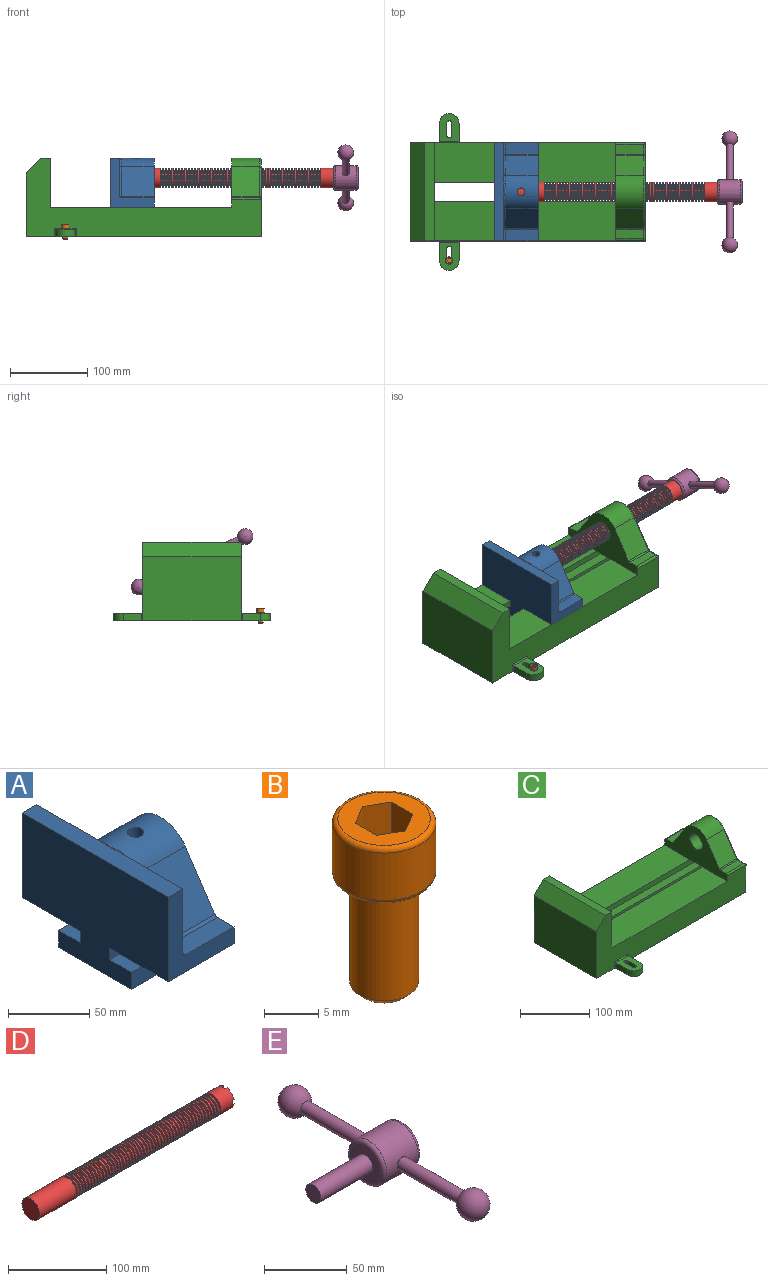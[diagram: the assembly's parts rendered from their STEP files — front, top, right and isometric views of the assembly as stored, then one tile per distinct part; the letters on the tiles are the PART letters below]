
ASSEMBLY  parts=5 mates=5
PART A: 36 faces, bbox 57.2x127x89 mm
  f0: plane 57.15x50.8mm, normal (0,0,-1), area 2903.2mm2, adj f6,f9,f10,f23
  f1: cylinder r=12.7mm len=44.45mm, axis (1,0,0), area 3464.3mm2, adj f6,f15,f16
  f2: plane 41.91x14.52mm, normal (0,0,1), area 608.5mm2, adj f6,f11,f24,f25
  f3: plane 51.86x48.26mm, normal (1,0,0), area 1495.7mm2, adj f8,f10,f31,f33,f35
  f4: plane 51.86x48.26mm, normal (1,0,0), area 1495.7mm2, adj f8,f11,f24,f28,f29
  f5: plane 57.15x50.8mm, normal (0,0,-1), area 2903.2mm2, adj f6,f9,f11,f22
  f6: plane 127x85.09mm, normal (1,0,0), area 5190.6mm2, adj f0,f1,f2,f5,f7,f10,f11,f12
  f7: plane 41.91x14.52mm, normal (0,0,1), area 608.5mm2, adj f6,f10,f30,f31
  f8: plane 127x12.7mm, normal (0,0,1), area 1612.9mm2, adj f3,f4,f9,f10,f11,f26,f34
  f9: plane 127x85.09mm, normal (-1,0,0), area 9096.8mm2, adj f0,f5,f8,f10,f11,f17,f18,f19
  f10: plane 63.5x57.15mm, normal (0,-1,0), area 1372.3mm2, adj f0,f3,f6,f7,f8,f9,f31
  f11: plane 63.5x57.15mm, normal (0,1,0), area 1372.3mm2, adj f2,f4,f5,f6,f8,f9,f24
  f12: plane 41.91x38.43mm, normal (0,-0.83,0.56), area 1939.2mm2, adj f6,f13,f30,f33
  f13: cylinder r=25.4mm len=44.45mm, axis (1,0,0), area 2026.5mm2, adj f6,f12,f14,f16,f26,f28,f34,f35
  f14: plane 41.91x38.43mm, normal (0,0.83,0.56), area 1939.2mm2, adj f6,f13,f25,f29
  f15: plane 25.4x25.4mm, normal (1,0,0), area 506.7mm2, adj f1
  f16: cylinder r=5.08mm len=13.76mm, axis (0,0,1), area 414mm2, adj f1,f13
  f17: plane 57.15x19.05mm, normal (0,0,1), area 1088.7mm2, adj f6,f9,f18,f23
  f18: plane 57.15x12.7mm, normal (0,-1,0), area 725.8mm2, adj f6,f9,f17,f19
  f19: plane 63.5x57.15mm, normal (0,0,-1), area 3629mm2, adj f6,f9,f18,f20
  f20: plane 57.15x12.7mm, normal (0,1,0), area 725.8mm2, adj f6,f9,f19,f21
  f21: plane 57.15x19.05mm, normal (0,0,1), area 1088.7mm2, adj f6,f9,f20,f22
  f22: plane 57.15x8.89mm, normal (0,1,0), area 508.1mm2, adj f5,f6,f9,f21
  f23: plane 57.15x8.89mm, normal (0,-1,0), area 508.1mm2, adj f0,f6,f9,f17
  f24: cylinder r=2.54mm len=14.52mm, axis (0,-1,0), area 57.9mm2, adj f2,f4,f11,f27
  f25: cylinder r=2.54mm len=41.91mm, axis (1,0,0), area 104.3mm2, adj f2,f6,f14,f27
  f26: bspline ~12.24x2.8mm, area 20.9mm2, adj f8,f13,f28
  f27: sphere r=2.54mm, area 6.3mm2, adj f24,f25,f29
  f28: torus R=27.94mm, axis (1,0,0), area 57.8mm2, adj f4,f13,f26,f29
  f29: cylinder r=2.54mm len=39.84mm, axis (0,-0.56,0.83), area 184.6mm2, adj f4,f14,f27,f28
  f30: cylinder r=2.54mm len=41.91mm, axis (1,0,0), area 104.3mm2, adj f6,f7,f12,f32
  f31: cylinder r=2.54mm len=14.52mm, axis (0,-1,0), area 57.9mm2, adj f3,f7,f10,f32
  f32: sphere r=2.54mm, area 6.3mm2, adj f30,f31,f33
  f33: cylinder r=2.54mm len=39.84mm, axis (0,-0.56,-0.83), area 184.6mm2, adj f3,f12,f32,f35
  f34: bspline ~12.24x2.8mm, area 20.9mm2, adj f8,f13,f35
  f35: torus R=27.94mm, axis (1,0,0), area 57.8mm2, adj f3,f13,f33,f34
PART B: 15 faces, bbox 10.3x10.3x19.1 mm
  f0: plane 8.51x8.51mm, normal (0,0,1), area 37.2mm2, adj f5,f6,f7,f8,f9,f10,f14
  f1: cylinder r=3.17mm len=11.94mm, axis (0,0,1), area 238.2mm2, adj f4,f12
  f2: plane 4.83x4.83mm, normal (0,0,-1), area 18.3mm2, adj f12
  f3: cylinder r=4.76mm len=9.53mm, axis (0,0,-1), area 159.6mm2, adj f13,f14
  f4: plane 8.51x8.51mm, normal (0,0,-1), area 25.2mm2, adj f1,f13
  f5: plane 4.83x2.38mm, normal (-0.5,-0.87,0), area 13.3mm2, adj f0,f6,f10,f11
  f6: plane 4.83x2.38mm, normal (0.5,-0.87,0), area 13.3mm2, adj f0,f5,f7,f11
  f7: plane 4.83x2.75mm, normal (1,0,0), area 13.3mm2, adj f0,f6,f8,f11
  f8: plane 4.83x2.38mm, normal (0.5,0.87,0), area 13.3mm2, adj f0,f7,f9,f11
  f9: plane 4.83x2.38mm, normal (-0.5,0.87,0), area 13.3mm2, adj f0,f8,f10,f11
  f10: plane 4.83x2.75mm, normal (-1,0,0), area 13.3mm2, adj f0,f5,f9,f11
  f11: plane 5.5x4.76mm, normal (0,0,1), area 19.6mm2, adj f5,f6,f7,f8,f9,f10
  f12: cone r=3.17mm half-angle=45deg, axis (0,0,1), area 18.9mm2, adj f1,f2
  f13: torus R=4.25mm, axis (0,0,1), area 23mm2, adj f3,f4
  f14: torus R=4.25mm, axis (0,0,1), area 23mm2, adj f0,f3
PART C: 61 faces, bbox 304.8x203.2x103.7 mm
  f0: plane 304.8x101.6mm, normal (0,1,0), area 13520.3mm2, adj f3,f4,f5,f6,f7,f8,f9,f16
  f1: plane 304.8x101.6mm, normal (0,-1,0), area 13520.3mm2, adj f2,f3,f5,f6,f7,f8,f9,f16
  f2: plane 234.95x50.8mm, normal (0,0,1), area 11935.5mm2, adj f1,f5,f16,f26
  f3: plane 127x99.06mm, normal (1,0,0), area 7097.5mm2, adj f0,f1,f9,f14,f17,f18,f19,f20
  f4: plane 234.95x50.8mm, normal (0,0,1), area 11935.5mm2, adj f0,f5,f16,f27
  f5: plane 127x101.6mm, normal (1,0,0), area 9516.1mm2, adj f0,f1,f2,f4,f6,f9,f18,f19
  f6: plane 127x12.7mm, normal (0,0,1), area 1612.9mm2, adj f0,f1,f5,f7
  f7: plane 127x19.05mm, normal (-0.71,0,0.71), area 3421.5mm2, adj f0,f1,f6,f8
  f8: plane 127x82.55mm, normal (-1,0,0), area 10483.8mm2, adj f0,f1,f7,f9
  f9: plane 304.8x203.2mm, normal (0,0,-1), area 33298.3mm2, adj f0,f1,f3,f5,f8,f21,f22,f39
  f10: plane 35.56x11.98mm, normal (0,0,1), area 426mm2, adj f16,f28,f29,f30
  f11: plane 38.43x35.56mm, normal (0,0.83,0.56), area 1645.4mm2, adj f12,f16,f29,f32
  f12: cylinder r=25.4mm len=42.19mm, axis (1,0,0), area 1770.2mm2, adj f11,f13,f16,f33
  f13: plane 38.43x35.56mm, normal (0,-0.83,0.56), area 1645.4mm2, adj f12,f16,f34,f35
  f14: cylinder r=12.7mm len=38.1mm, axis (1,0,0), area 3040.2mm2, adj f3,f16
  f15: plane 35.56x11.98mm, normal (0,0,1), area 426mm2, adj f16,f34,f36,f38
  f16: plane 127x63.5mm, normal (-1,0,0), area 4155.5mm2, adj f0,f1,f2,f4,f10,f11,f12,f13
  f17: plane 38.1x25.4mm, normal (0,0,-1), area 967.7mm2, adj f3,f16,f26,f27
  f18: plane 273.05x19.05mm, normal (0,0,-1), area 5201.6mm2, adj f3,f5,f19,f26
  f19: plane 273.05x12.7mm, normal (0,1,0), area 3467.7mm2, adj f3,f5,f18,f20
  f20: plane 273.05x19.05mm, normal (0,0,1), area 5201.6mm2, adj f3,f5,f19,f21
  f21: plane 273.05x16.51mm, normal (0,1,0), area 4508.1mm2, adj f3,f5,f9,f20
  f22: plane 273.05x16.51mm, normal (0,-1,0), area 4508.1mm2, adj f3,f5,f9,f23
  f23: plane 273.05x19.05mm, normal (0,0,1), area 5201.6mm2, adj f3,f5,f22,f24
  f24: plane 273.05x12.7mm, normal (0,-1,0), area 3467.7mm2, adj f3,f5,f23,f25
  f25: plane 273.05x19.05mm, normal (0,0,-1), area 5201.6mm2, adj f3,f5,f24,f27
  f26: plane 273.05x8.89mm, normal (0,1,0), area 2427.4mm2, adj f2,f3,f5,f17,f18
  f27: plane 273.05x8.89mm, normal (0,-1,0), area 2427.4mm2, adj f3,f4,f5,f17,f25
  f28: cylinder r=2.54mm len=38.1mm, axis (1,0,0), area 148.3mm2, adj f0,f10,f16,f30
  f29: cylinder r=2.54mm len=35.56mm, axis (-1,0,0), area 88.5mm2, adj f10,f11,f16,f31
  f30: cylinder r=2.54mm len=14.52mm, axis (0,1,0), area 54.3mm2, adj f3,f10,f28,f31
  f31: torus R=5.08mm, axis (-1,0,0), area 13.5mm2, adj f3,f29,f30,f32
  f32: cylinder r=2.54mm len=39.84mm, axis (0,0.56,-0.83), area 184.6mm2, adj f3,f11,f31,f33
  f33: torus R=22.86mm, axis (-1,0,0), area 191.4mm2, adj f3,f12,f32,f35
  f34: cylinder r=2.54mm len=35.56mm, axis (-1,0,0), area 88.5mm2, adj f13,f15,f16,f37
  f35: cylinder r=2.54mm len=39.84mm, axis (0,0.56,0.83), area 184.6mm2, adj f3,f13,f33,f37
  f36: cylinder r=2.54mm len=38.1mm, axis (-1,0,0), area 148.3mm2, adj f1,f15,f16,f38
  f37: torus R=5.08mm, axis (-1,0,0), area 13.5mm2, adj f3,f34,f35,f38
  f38: cylinder r=2.54mm len=14.52mm, axis (0,1,0), area 54.3mm2, adj f3,f15,f36,f37
  f39: plane 23.88x9.53mm, normal (-1,0,0), area 227.4mm2, adj f9,f45,f46,f60
  f40: plane 23.88x9.53mm, normal (1,0,0), area 227.4mm2, adj f9,f45,f46,f58
  f41: cylinder r=3.3mm len=9.53mm, axis (0,0,-1), area 98.8mm2, adj f9,f42,f44,f46
  f42: plane 15.62x9.53mm, normal (-1,0,0), area 148.8mm2, adj f9,f41,f43,f46
  f43: cylinder r=3.3mm len=9.53mm, axis (0,0,-1), area 98.8mm2, adj f9,f42,f44,f46
  f44: plane 15.62x9.53mm, normal (1,0,0), area 148.8mm2, adj f9,f41,f43,f46
  f45: cylinder r=12.7mm len=25.4mm, axis (0,0,-1), area 380mm2, adj f9,f39,f40,f46
  f46: plane 36.58x25.4mm, normal (0,0,1), area 722.4mm2, adj f39,f40,f41,f42,f43,f44,f45,f59
  f47: plane 23.88x9.53mm, normal (-1,0,0), area 227.4mm2, adj f9,f53,f54,f56
  f48: plane 23.88x9.53mm, normal (1,0,0), area 227.4mm2, adj f9,f53,f54,f55
  f49: cylinder r=3.3mm len=9.53mm, axis (0,0,-1), area 98.8mm2, adj f9,f50,f52,f54
  f50: plane 15.62x9.53mm, normal (-1,0,0), area 148.8mm2, adj f9,f49,f51,f54
  f51: cylinder r=3.3mm len=9.53mm, axis (0,0,-1), area 98.8mm2, adj f9,f50,f52,f54
  f52: plane 15.62x9.53mm, normal (1,0,0), area 148.8mm2, adj f9,f49,f51,f54
  f53: cylinder r=12.7mm len=25.4mm, axis (0,0,-1), area 380mm2, adj f9,f47,f48,f54
  f54: plane 36.58x25.4mm, normal (0,0,1), area 722.4mm2, adj f47,f48,f49,f50,f51,f52,f53,f57
  f55: cylinder r=1.52mm len=11.05mm, axis (0,0,-1), area 24.1mm2, adj f0,f9,f48,f57
  f56: cylinder r=1.52mm len=11.05mm, axis (0,0,1), area 24.1mm2, adj f0,f9,f47,f57
  f57: cylinder r=1.52mm len=28.45mm, axis (1,0,0), area 63.5mm2, adj f0,f54,f55,f56
  f58: cylinder r=1.52mm len=11.05mm, axis (0,0,1), area 24.1mm2, adj f1,f9,f40,f59
  f59: cylinder r=1.52mm len=28.45mm, axis (-1,0,0), area 63.5mm2, adj f1,f46,f58,f60
  f60: cylinder r=1.52mm len=11.05mm, axis (0,0,-1), area 24.1mm2, adj f1,f9,f39,f59
PART D: 220 faces, bbox 279.4x25.4x25.4 mm
  f0: cylinder r=12.7mm len=25.4mm, axis (-1,0,0), area 1468.2mm2, adj f1,f2,f3,f5,f7,f208,f209,f210
  f1: plane 9.9x9.9mm, normal (1,0,0), area 62.3mm2, adj f0,f4,f213,f216
  f2: plane 9.9x9.9mm, normal (1,0,0), area 62.3mm2, adj f0,f4,f210,f218
  f3: plane 9.9x9.9mm, normal (1,0,0), area 62.3mm2, adj f0,f4,f209,f212
  f4: cylinder r=6.35mm len=25.4mm, axis (1,0,0), area 960.3mm2, adj f1,f2,f3,f5,f6,f208,f209,f210
  f5: plane 9.9x9.9mm, normal (1,0,0), area 62.3mm2, adj f0,f4,f215,f217
  f6: plane 12.7x12.7mm, normal (1,0,0), area 126.7mm2, adj f4
  f7: cone r=12.7mm half-angle=76deg, axis (1,0,0), area 188mm2, adj f0,f9
  f8: cone r=10.16mm half-angle=76deg, axis (-1,0,0), area 188mm2, adj f9,f10
  f9: cylinder r=10.16mm len=20.32mm, axis (1,0,0), area 81.1mm2, adj f7,f8
  f10: cylinder r=12.7mm len=25.4mm, axis (-1,0,0), area 131.7mm2, adj f8,f11
  f11: cone r=12.7mm half-angle=76deg, axis (1,0,0), area 188mm2, adj f10,f13
  f12: cone r=10.16mm half-angle=76deg, axis (-1,0,0), area 188mm2, adj f13,f14
  f13: cylinder r=10.16mm len=20.32mm, axis (1,0,0), area 81.1mm2, adj f11,f12
  f14: cylinder r=12.7mm len=25.4mm, axis (-1,0,0), area 131.7mm2, adj f12,f15
  f15: cone r=12.7mm half-angle=76deg, axis (1,0,0), area 188mm2, adj f14,f17
  f16: cone r=10.16mm half-angle=76deg, axis (-1,0,0), area 188mm2, adj f17,f18
  f17: cylinder r=10.16mm len=20.32mm, axis (1,0,0), area 81.1mm2, adj f15,f16
  f18: cylinder r=12.7mm len=25.4mm, axis (-1,0,0), area 131.7mm2, adj f16,f19
  f19: cone r=12.7mm half-angle=76deg, axis (1,0,0), area 188mm2, adj f18,f21
  f20: cone r=10.16mm half-angle=76deg, axis (-1,0,0), area 188mm2, adj f21,f22
  f21: cylinder r=10.16mm len=20.32mm, axis (1,0,0), area 81.1mm2, adj f19,f20
  f22: cylinder r=12.7mm len=25.4mm, axis (-1,0,0), area 131.7mm2, adj f20,f23
  f23: cone r=12.7mm half-angle=76deg, axis (1,0,0), area 188mm2, adj f22,f25
  f24: cone r=10.16mm half-angle=76deg, axis (-1,0,0), area 188mm2, adj f25,f26
  f25: cylinder r=10.16mm len=20.32mm, axis (1,0,0), area 81.1mm2, adj f23,f24
  f26: cylinder r=12.7mm len=25.4mm, axis (-1,0,0), area 131.7mm2, adj f24,f27
  f27: cone r=12.7mm half-angle=76deg, axis (1,0,0), area 188mm2, adj f26,f29
  f28: cone r=10.16mm half-angle=76deg, axis (-1,0,0), area 188mm2, adj f29,f30
  f29: cylinder r=10.16mm len=20.32mm, axis (1,0,0), area 81.1mm2, adj f27,f28
  f30: cylinder r=12.7mm len=25.4mm, axis (-1,0,0), area 131.7mm2, adj f28,f31
  f31: cone r=12.7mm half-angle=76deg, axis (1,0,0), area 188mm2, adj f30,f33
  f32: cone r=10.16mm half-angle=76deg, axis (-1,0,0), area 188mm2, adj f33,f34
  f33: cylinder r=10.16mm len=20.32mm, axis (1,0,0), area 81.1mm2, adj f31,f32
  f34: cylinder r=12.7mm len=25.4mm, axis (-1,0,0), area 131.7mm2, adj f32,f35
  f35: cone r=12.7mm half-angle=76deg, axis (1,0,0), area 188mm2, adj f34,f37
  f36: cone r=10.16mm half-angle=76deg, axis (-1,0,0), area 188mm2, adj f37,f38
  f37: cylinder r=10.16mm len=20.32mm, axis (1,0,0), area 81.1mm2, adj f35,f36
  f38: cylinder r=12.7mm len=25.4mm, axis (-1,0,0), area 131.7mm2, adj f36,f39
  f39: cone r=12.7mm half-angle=76deg, axis (1,0,0), area 188mm2, adj f38,f41
  f40: cone r=10.16mm half-angle=76deg, axis (-1,0,0), area 188mm2, adj f41,f42
  f41: cylinder r=10.16mm len=20.32mm, axis (1,0,0), area 81.1mm2, adj f39,f40
  f42: cylinder r=12.7mm len=25.4mm, axis (-1,0,0), area 131.7mm2, adj f40,f43
  f43: cone r=12.7mm half-angle=76deg, axis (1,0,0), area 188mm2, adj f42,f45
  f44: cone r=10.16mm half-angle=76deg, axis (-1,0,0), area 188mm2, adj f45,f46
  f45: cylinder r=10.16mm len=20.32mm, axis (1,0,0), area 81.1mm2, adj f43,f44
  f46: cylinder r=12.7mm len=25.4mm, axis (-1,0,0), area 131.7mm2, adj f44,f47
  f47: cone r=12.7mm half-angle=76deg, axis (1,0,0), area 188mm2, adj f46,f49
  f48: cone r=10.16mm half-angle=76deg, axis (-1,0,0), area 188mm2, adj f49,f50
  f49: cylinder r=10.16mm len=20.32mm, axis (1,0,0), area 81.1mm2, adj f47,f48
  f50: cylinder r=12.7mm len=25.4mm, axis (-1,0,0), area 131.7mm2, adj f48,f51
  f51: cone r=12.7mm half-angle=76deg, axis (1,0,0), area 188mm2, adj f50,f53
  f52: cone r=10.16mm half-angle=76deg, axis (-1,0,0), area 188mm2, adj f53,f54
  f53: cylinder r=10.16mm len=20.32mm, axis (1,0,0), area 81.1mm2, adj f51,f52
  f54: cylinder r=12.7mm len=25.4mm, axis (-1,0,0), area 131.7mm2, adj f52,f55
  f55: cone r=12.7mm half-angle=76deg, axis (1,0,0), area 188mm2, adj f54,f57
  f56: cone r=10.16mm half-angle=76deg, axis (-1,0,0), area 188mm2, adj f57,f58
  f57: cylinder r=10.16mm len=20.32mm, axis (1,0,0), area 81.1mm2, adj f55,f56
  f58: cylinder r=12.7mm len=25.4mm, axis (-1,0,0), area 131.7mm2, adj f56,f59
  f59: cone r=12.7mm half-angle=76deg, axis (1,0,0), area 188mm2, adj f58,f61
  f60: cone r=10.16mm half-angle=76deg, axis (-1,0,0), area 188mm2, adj f61,f62
  f61: cylinder r=10.16mm len=20.32mm, axis (1,0,0), area 81.1mm2, adj f59,f60
  f62: cylinder r=12.7mm len=25.4mm, axis (-1,0,0), area 131.7mm2, adj f60,f63
  f63: cone r=12.7mm half-angle=76deg, axis (1,0,0), area 188mm2, adj f62,f65
  f64: cone r=10.16mm half-angle=76deg, axis (-1,0,0), area 188mm2, adj f65,f66
  f65: cylinder r=10.16mm len=20.32mm, axis (1,0,0), area 81.1mm2, adj f63,f64
  f66: cylinder r=12.7mm len=25.4mm, axis (-1,0,0), area 131.7mm2, adj f64,f67
  f67: cone r=12.7mm half-angle=76deg, axis (1,0,0), area 188mm2, adj f66,f69
  f68: cone r=10.16mm half-angle=76deg, axis (-1,0,0), area 188mm2, adj f69,f70
  f69: cylinder r=10.16mm len=20.32mm, axis (1,0,0), area 81.1mm2, adj f67,f68
  f70: cylinder r=12.7mm len=25.4mm, axis (-1,0,0), area 131.7mm2, adj f68,f71
  f71: cone r=12.7mm half-angle=76deg, axis (1,0,0), area 188mm2, adj f70,f73
  f72: cone r=10.16mm half-angle=76deg, axis (-1,0,0), area 188mm2, adj f73,f74
  f73: cylinder r=10.16mm len=20.32mm, axis (1,0,0), area 81.1mm2, adj f71,f72
  f74: cylinder r=12.7mm len=25.4mm, axis (-1,0,0), area 131.7mm2, adj f72,f75
  f75: cone r=12.7mm half-angle=76deg, axis (1,0,0), area 188mm2, adj f74,f77
  f76: cone r=10.16mm half-angle=76deg, axis (-1,0,0), area 188mm2, adj f77,f78
  f77: cylinder r=10.16mm len=20.32mm, axis (1,0,0), area 81.1mm2, adj f75,f76
  f78: cylinder r=12.7mm len=25.4mm, axis (-1,0,0), area 131.7mm2, adj f76,f79
  f79: cone r=12.7mm half-angle=76deg, axis (1,0,0), area 188mm2, adj f78,f81
  f80: cone r=10.16mm half-angle=76deg, axis (-1,0,0), area 188mm2, adj f81,f82
  f81: cylinder r=10.16mm len=20.32mm, axis (1,0,0), area 81.1mm2, adj f79,f80
  f82: cylinder r=12.7mm len=25.4mm, axis (-1,0,0), area 131.7mm2, adj f80,f83
  f83: cone r=12.7mm half-angle=76deg, axis (1,0,0), area 188mm2, adj f82,f85
  f84: cone r=10.16mm half-angle=76deg, axis (-1,0,0), area 188mm2, adj f85,f86
  f85: cylinder r=10.16mm len=20.32mm, axis (1,0,0), area 81.1mm2, adj f83,f84
  f86: cylinder r=12.7mm len=25.4mm, axis (-1,0,0), area 131.7mm2, adj f84,f87
  f87: cone r=12.7mm half-angle=76deg, axis (1,0,0), area 188mm2, adj f86,f89
  f88: cone r=10.16mm half-angle=76deg, axis (-1,0,0), area 188mm2, adj f89,f90
  f89: cylinder r=10.16mm len=20.32mm, axis (1,0,0), area 81.1mm2, adj f87,f88
  f90: cylinder r=12.7mm len=25.4mm, axis (-1,0,0), area 131.7mm2, adj f88,f91
  f91: cone r=12.7mm half-angle=76deg, axis (1,0,0), area 188mm2, adj f90,f93
  f92: cone r=10.16mm half-angle=76deg, axis (-1,0,0), area 188mm2, adj f93,f94
  f93: cylinder r=10.16mm len=20.32mm, axis (1,0,0), area 81.1mm2, adj f91,f92
  f94: cylinder r=12.7mm len=25.4mm, axis (-1,0,0), area 131.7mm2, adj f92,f95
  f95: cone r=12.7mm half-angle=76deg, axis (1,0,0), area 188mm2, adj f94,f97
  f96: cone r=10.16mm half-angle=76deg, axis (-1,0,0), area 188mm2, adj f97,f98
  f97: cylinder r=10.16mm len=20.32mm, axis (1,0,0), area 81.1mm2, adj f95,f96
  f98: cylinder r=12.7mm len=25.4mm, axis (-1,0,0), area 131.7mm2, adj f96,f99
  f99: cone r=12.7mm half-angle=76deg, axis (1,0,0), area 188mm2, adj f98,f101
  f100: cone r=10.16mm half-angle=76deg, axis (-1,0,0), area 188mm2, adj f101,f102
  f101: cylinder r=10.16mm len=20.32mm, axis (1,0,0), area 81.1mm2, adj f99,f100
  f102: cylinder r=12.7mm len=25.4mm, axis (-1,0,0), area 131.7mm2, adj f100,f103
  f103: cone r=12.7mm half-angle=76deg, axis (1,0,0), area 188mm2, adj f102,f105
  f104: cone r=10.16mm half-angle=76deg, axis (-1,0,0), area 188mm2, adj f105,f106
  f105: cylinder r=10.16mm len=20.32mm, axis (1,0,0), area 81.1mm2, adj f103,f104
  f106: cylinder r=12.7mm len=25.4mm, axis (-1,0,0), area 131.7mm2, adj f104,f107
  f107: cone r=12.7mm half-angle=76deg, axis (1,0,0), area 188mm2, adj f106,f109
  f108: cone r=10.16mm half-angle=76deg, axis (-1,0,0), area 188mm2, adj f109,f110
  f109: cylinder r=10.16mm len=20.32mm, axis (1,0,0), area 81.1mm2, adj f107,f108
  f110: cylinder r=12.7mm len=25.4mm, axis (-1,0,0), area 131.7mm2, adj f108,f111
  f111: cone r=12.7mm half-angle=76deg, axis (1,0,0), area 188mm2, adj f110,f113
  f112: cone r=10.16mm half-angle=76deg, axis (-1,0,0), area 188mm2, adj f113,f114
  f113: cylinder r=10.16mm len=20.32mm, axis (1,0,0), area 81.1mm2, adj f111,f112
  f114: cylinder r=12.7mm len=25.4mm, axis (-1,0,0), area 131.7mm2, adj f112,f115
  f115: cone r=12.7mm half-angle=76deg, axis (1,0,0), area 188mm2, adj f114,f117
  f116: cone r=10.16mm half-angle=76deg, axis (-1,0,0), area 188mm2, adj f117,f118
  f117: cylinder r=10.16mm len=20.32mm, axis (1,0,0), area 81.1mm2, adj f115,f116
  f118: cylinder r=12.7mm len=25.4mm, axis (-1,0,0), area 131.7mm2, adj f116,f119
  f119: cone r=12.7mm half-angle=76deg, axis (1,0,0), area 188mm2, adj f118,f121
  f120: cone r=10.16mm half-angle=76deg, axis (-1,0,0), area 188mm2, adj f121,f122
  f121: cylinder r=10.16mm len=20.32mm, axis (1,0,0), area 81.1mm2, adj f119,f120
  f122: cylinder r=12.7mm len=25.4mm, axis (-1,0,0), area 131.7mm2, adj f120,f123
  f123: cone r=12.7mm half-angle=76deg, axis (1,0,0), area 188mm2, adj f122,f125
  f124: cone r=10.16mm half-angle=76deg, axis (-1,0,0), area 188mm2, adj f125,f126
  f125: cylinder r=10.16mm len=20.32mm, axis (1,0,0), area 81.1mm2, adj f123,f124
  f126: cylinder r=12.7mm len=25.4mm, axis (-1,0,0), area 131.7mm2, adj f124,f127
  f127: cone r=12.7mm half-angle=76deg, axis (1,0,0), area 188mm2, adj f126,f129
  f128: cone r=10.16mm half-angle=76deg, axis (-1,0,0), area 188mm2, adj f129,f130
  f129: cylinder r=10.16mm len=20.32mm, axis (1,0,0), area 81.1mm2, adj f127,f128
  f130: cylinder r=12.7mm len=25.4mm, axis (-1,0,0), area 131.7mm2, adj f128,f131
  f131: cone r=12.7mm half-angle=76deg, axis (1,0,0), area 188mm2, adj f130,f133
  f132: cone r=10.16mm half-angle=76deg, axis (-1,0,0), area 188mm2, adj f133,f134
  f133: cylinder r=10.16mm len=20.32mm, axis (1,0,0), area 81.1mm2, adj f131,f132
  f134: cylinder r=12.7mm len=25.4mm, axis (-1,0,0), area 131.7mm2, adj f132,f135
  f135: cone r=12.7mm half-angle=76deg, axis (1,0,0), area 188mm2, adj f134,f137
  f136: cone r=10.16mm half-angle=76deg, axis (-1,0,0), area 188mm2, adj f137,f138
  f137: cylinder r=10.16mm len=20.32mm, axis (1,0,0), area 81.1mm2, adj f135,f136
  f138: cylinder r=12.7mm len=25.4mm, axis (-1,0,0), area 131.7mm2, adj f136,f139
  f139: cone r=12.7mm half-angle=76deg, axis (1,0,0), area 188mm2, adj f138,f141
  f140: cone r=10.16mm half-angle=76deg, axis (-1,0,0), area 188mm2, adj f141,f142
  f141: cylinder r=10.16mm len=20.32mm, axis (1,0,0), area 81.1mm2, adj f139,f140
  f142: cylinder r=12.7mm len=25.4mm, axis (-1,0,0), area 131.7mm2, adj f140,f143
  f143: cone r=12.7mm half-angle=76deg, axis (1,0,0), area 188mm2, adj f142,f145
  f144: cone r=10.16mm half-angle=76deg, axis (-1,0,0), area 188mm2, adj f145,f146
  f145: cylinder r=10.16mm len=20.32mm, axis (1,0,0), area 81.1mm2, adj f143,f144
  f146: cylinder r=12.7mm len=25.4mm, axis (-1,0,0), area 131.7mm2, adj f144,f147
  f147: cone r=12.7mm half-angle=76deg, axis (1,0,0), area 188mm2, adj f146,f149
  f148: cone r=10.16mm half-angle=76deg, axis (-1,0,0), area 188mm2, adj f149,f150
  f149: cylinder r=10.16mm len=20.32mm, axis (1,0,0), area 81.1mm2, adj f147,f148
  f150: cylinder r=12.7mm len=25.4mm, axis (-1,0,0), area 131.7mm2, adj f148,f151
  f151: cone r=12.7mm half-angle=76deg, axis (1,0,0), area 188mm2, adj f150,f153
  f152: cone r=10.16mm half-angle=76deg, axis (-1,0,0), area 188mm2, adj f153,f154
  f153: cylinder r=10.16mm len=20.32mm, axis (1,0,0), area 81.1mm2, adj f151,f152
  f154: cylinder r=12.7mm len=25.4mm, axis (-1,0,0), area 131.7mm2, adj f152,f155
  f155: cone r=12.7mm half-angle=76deg, axis (1,0,0), area 188mm2, adj f154,f157
  f156: cone r=10.16mm half-angle=76deg, axis (-1,0,0), area 188mm2, adj f157,f158
  f157: cylinder r=10.16mm len=20.32mm, axis (1,0,0), area 81.1mm2, adj f155,f156
  f158: cylinder r=12.7mm len=25.4mm, axis (-1,0,0), area 131.7mm2, adj f156,f159
  f159: cone r=12.7mm half-angle=76deg, axis (1,0,0), area 188mm2, adj f158,f161
  f160: cone r=10.16mm half-angle=76deg, axis (-1,0,0), area 188mm2, adj f161,f162
  f161: cylinder r=10.16mm len=20.32mm, axis (1,0,0), area 81.1mm2, adj f159,f160
  f162: cylinder r=12.7mm len=25.4mm, axis (-1,0,0), area 131.7mm2, adj f160,f163
  f163: cone r=12.7mm half-angle=76deg, axis (1,0,0), area 188mm2, adj f162,f165
  f164: cone r=10.16mm half-angle=76deg, axis (-1,0,0), area 188mm2, adj f165,f166
  f165: cylinder r=10.16mm len=20.32mm, axis (1,0,0), area 81.1mm2, adj f163,f164
  f166: cylinder r=12.7mm len=25.4mm, axis (-1,0,0), area 131.7mm2, adj f164,f167
  f167: cone r=12.7mm half-angle=76deg, axis (1,0,0), area 188mm2, adj f166,f169
  f168: cone r=10.16mm half-angle=76deg, axis (-1,0,0), area 188mm2, adj f169,f170
  f169: cylinder r=10.16mm len=20.32mm, axis (1,0,0), area 81.1mm2, adj f167,f168
  f170: cylinder r=12.7mm len=25.4mm, axis (-1,0,0), area 131.7mm2, adj f168,f171
  f171: cone r=12.7mm half-angle=76deg, axis (1,0,0), area 188mm2, adj f170,f173
  f172: cone r=10.16mm half-angle=76deg, axis (-1,0,0), area 188mm2, adj f173,f174
  f173: cylinder r=10.16mm len=20.32mm, axis (1,0,0), area 81.1mm2, adj f171,f172
  f174: cylinder r=12.7mm len=25.4mm, axis (-1,0,0), area 131.7mm2, adj f172,f175
  f175: cone r=12.7mm half-angle=76deg, axis (1,0,0), area 188mm2, adj f174,f177
  f176: cone r=10.16mm half-angle=76deg, axis (-1,0,0), area 188mm2, adj f177,f178
  f177: cylinder r=10.16mm len=20.32mm, axis (1,0,0), area 81.1mm2, adj f175,f176
  f178: cylinder r=12.7mm len=25.4mm, axis (-1,0,0), area 131.7mm2, adj f176,f179
  f179: cone r=12.7mm half-angle=76deg, axis (1,0,0), area 188mm2, adj f178,f181
  f180: cone r=10.16mm half-angle=76deg, axis (-1,0,0), area 188mm2, adj f181,f182
  f181: cylinder r=10.16mm len=20.32mm, axis (1,0,0), area 81.1mm2, adj f179,f180
  f182: cylinder r=12.7mm len=25.4mm, axis (-1,0,0), area 131.7mm2, adj f180,f183
  f183: cone r=12.7mm half-angle=76deg, axis (1,0,0), area 188mm2, adj f182,f185
  f184: cone r=10.16mm half-angle=76deg, axis (-1,0,0), area 188mm2, adj f185,f186
  f185: cylinder r=10.16mm len=20.32mm, axis (1,0,0), area 81.1mm2, adj f183,f184
  f186: cylinder r=12.7mm len=25.4mm, axis (-1,0,0), area 131.7mm2, adj f184,f187
  f187: cone r=12.7mm half-angle=76deg, axis (1,0,0), area 188mm2, adj f186,f189
  f188: cone r=10.16mm half-angle=76deg, axis (-1,0,0), area 188mm2, adj f189,f190
  f189: cylinder r=10.16mm len=20.32mm, axis (1,0,0), area 81.1mm2, adj f187,f188
  f190: cylinder r=12.7mm len=25.4mm, axis (-1,0,0), area 131.7mm2, adj f188,f191
  f191: cone r=12.7mm half-angle=76deg, axis (1,0,0), area 188mm2, adj f190,f193
  f192: cone r=10.16mm half-angle=76deg, axis (-1,0,0), area 188mm2, adj f193,f194
  f193: cylinder r=10.16mm len=20.32mm, axis (1,0,0), area 81.1mm2, adj f191,f192
  f194: cylinder r=12.7mm len=25.4mm, axis (-1,0,0), area 131.7mm2, adj f192,f195
  f195: cone r=12.7mm half-angle=76deg, axis (1,0,0), area 188mm2, adj f194,f197
  f196: cone r=10.16mm half-angle=76deg, axis (-1,0,0), area 188mm2, adj f197,f198
  f197: cylinder r=10.16mm len=20.32mm, axis (1,0,0), area 81.1mm2, adj f195,f196
  f198: cylinder r=12.7mm len=25.4mm, axis (-1,0,0), area 131.7mm2, adj f196,f199
  f199: cone r=12.7mm half-angle=76deg, axis (1,0,0), area 188mm2, adj f198,f201
  f200: cone r=10.16mm half-angle=76deg, axis (-1,0,0), area 188mm2, adj f201,f202
  f201: cylinder r=10.16mm len=20.32mm, axis (1,0,0), area 81.1mm2, adj f199,f200
  f202: cylinder r=12.7mm len=25.4mm, axis (-1,0,0), area 131.7mm2, adj f200,f203
  f203: cone r=12.7mm half-angle=76deg, axis (1,0,0), area 188mm2, adj f202,f205
  f204: cone r=10.16mm half-angle=76deg, axis (-1,0,0), area 188mm2, adj f205,f207
  f205: cylinder r=10.16mm len=20.32mm, axis (1,0,0), area 81.1mm2, adj f203,f204
  f206: plane 25.4x25.4mm, normal (-1,0,0), area 506.7mm2, adj f207
  f207: cylinder r=12.7mm len=52.45mm, axis (-1,0,0), area 4185.4mm2, adj f204,f206
  f208: plane 6.88x5.08mm, normal (1,0,0), area 32.7mm2, adj f0,f4,f209,f210
  f209: plane 6.62x2.54mm, normal (0,-1,0), area 16.8mm2, adj f0,f3,f4,f208
  f210: plane 6.62x2.54mm, normal (0,1,0), area 16.8mm2, adj f0,f2,f4,f208
  f211: plane 6.88x5.08mm, normal (1,0,0), area 32.7mm2, adj f0,f4,f212,f213
  f212: plane 6.62x2.54mm, normal (0,0,1), area 16.8mm2, adj f0,f3,f4,f211
  f213: plane 6.62x2.54mm, normal (0,0,-1), area 16.8mm2, adj f0,f1,f4,f211
  f214: plane 6.88x5.08mm, normal (1,0,0), area 32.7mm2, adj f0,f4,f215,f216
  f215: plane 6.62x2.54mm, normal (0,1,0), area 16.8mm2, adj f0,f4,f5,f214
  f216: plane 6.62x2.54mm, normal (0,-1,0), area 16.8mm2, adj f0,f1,f4,f214
  f217: plane 6.62x2.54mm, normal (0,0,-1), area 16.8mm2, adj f0,f4,f5,f219
  f218: plane 6.62x2.54mm, normal (0,0,1), area 16.8mm2, adj f0,f2,f4,f219
  f219: plane 6.88x5.08mm, normal (1,0,0), area 32.7mm2, adj f0,f4,f217,f218
PART E: 11 faces, bbox 76.2x172.7x34.4 mm
  f0: sphere r=10.16mm, area 1231.8mm2, adj f1
  f1: cylinder r=4.45mm len=51.82mm, axis (0,1,0), area 1438.5mm2, adj f0,f4
  f2: sphere r=10.16mm, area 1231.8mm2, adj f3
  f3: cylinder r=4.45mm len=51.82mm, axis (0,1,0), area 1438.5mm2, adj f2,f4
  f4: cylinder r=15.88mm len=31.75mm, axis (-1,0,0), area 2534.7mm2, adj f1,f3,f9,f10
  f5: cylinder r=6.35mm len=44.45mm, axis (-1,0,0), area 1773.5mm2, adj f6,f8
  f6: plane 12.7x12.7mm, normal (-1,0,0), area 126.7mm2, adj f5
  f7: plane 26.67x26.67mm, normal (1,0,0), area 558.6mm2, adj f10
  f8: plane 26.67x26.67mm, normal (-1,0,0), area 432mm2, adj f5,f9
  f9: torus R=13.33mm, axis (1,0,0), area 374.8mm2, adj f4,f8
  f10: torus R=13.33mm, axis (1,0,0), area 374.8mm2, adj f4,f7
PLACE A t=(77.09,0,0)mm
PLACE B rot(axis=(0,0,1),90deg) t=(-254,-88.9,9.52)mm
PLACE C at identity fixed
PLACE D rot(axis=(1,0,0),154.7deg) t=(77.09,32.62,145.07)mm
PLACE E rot(axis=(1,0,0),154.7deg) t=(55.5,32.62,145.07)mm
MATE fastened D.f4 <-> E.f5  axis (1,0,0) through (93.6,0,76.2)mm
MATE planar A.f0 <-> C.f2  axis (0,0,-1) through (-167.38,-38.1,38.1)mm
MATE pin_slot B.f1 <-> C.f41  axis (0,0,1) through (-254,-88.9,9.52)mm
MATE revolute D.f7 <-> A.f28  axis (-1,0,0) through (-183.26,0,76.2)mm
MATE cylindrical C.f12 <-> D.f7  axis (-1,0,0) through (-38.1,0,76.2)mm
